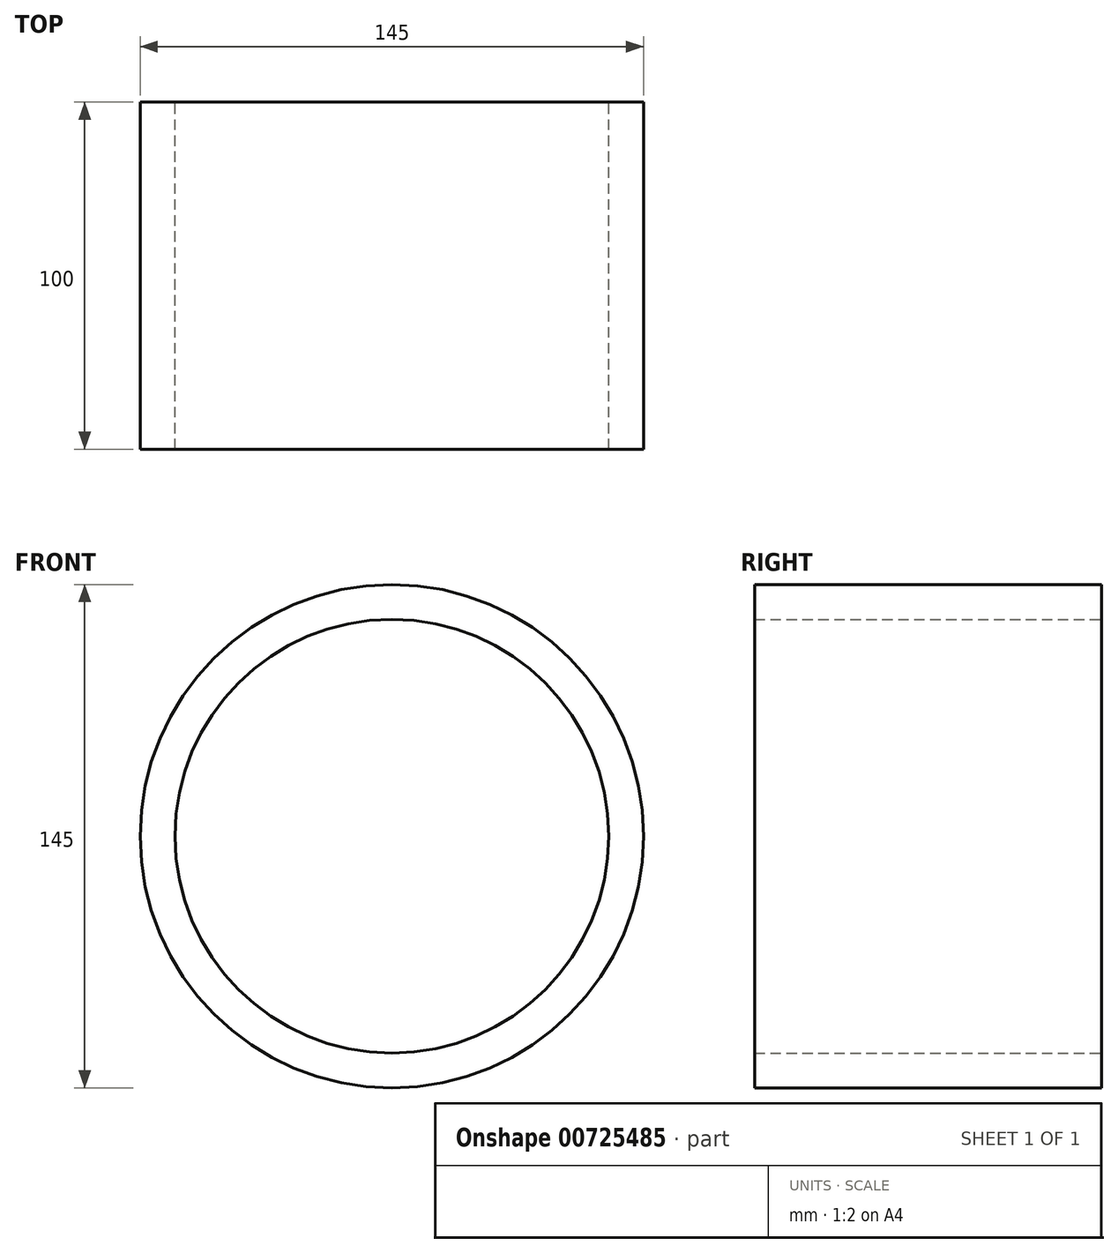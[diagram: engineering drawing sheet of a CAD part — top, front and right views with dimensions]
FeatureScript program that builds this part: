
annotation { "Feature Type Name" : "Feature", "Feature Type Description" : "" }
export const myFeature = defineFeature(function(context is Context, id is Id, definition is map)
    precondition{}
    {
        {
            var Q0;
            Q0=qCreatedBy(makeId("Front.planeOp"),FACE);
            var sketch = newSketch(context, id + "F0", { "sketchPlane" : qUnion([Q0])});
            skCircle(sketch, "E0", {"center": v(0, 0) * mm, "radius": 62.5 * mm});
            skCircle(sketch, "E1.0", {"center": v(0, 0) * mm, "radius": 72.5 * mm});
            skSolve(sketch);
        }
        {
            var Q0;
            Q0=makeQuery(id+"F0.imprint","IMPRINT",FACE,{"disambiguationData":[TD([[makeQuery(id+"F0.imprint","IMPRINT",EDGE,{"derivedFrom":sQuery(id+"F0.wireOp",EDGE,"E0")}),-1.0]])]});
            extrude(context, id + "F1", {"entities" : qUnion([Q0]), "depth" : 50 * mm, "offsetDistance" : 25 * mm});
        }
        {
            var Q0;
            Q0=makeQuery(id+"F1.opExtrude","SWEPT_BODY",BODY,{"disambiguationData":[OSD([sQuery(id+"F0.wireOp",EDGE,"E0"),sQuery(id+"F0.wireOp",EDGE,"E1.0")])]});
            var Q1;
            Q1=qCreatedBy(makeId("Front.planeOp"),FACE);
            mirror(context, id + "F2", {"operationType" : NewBodyOperationType.ADD, "entities" : qUnion([Q0]), "mirrorPlane" : qUnion([Q1])});
        }
    });
